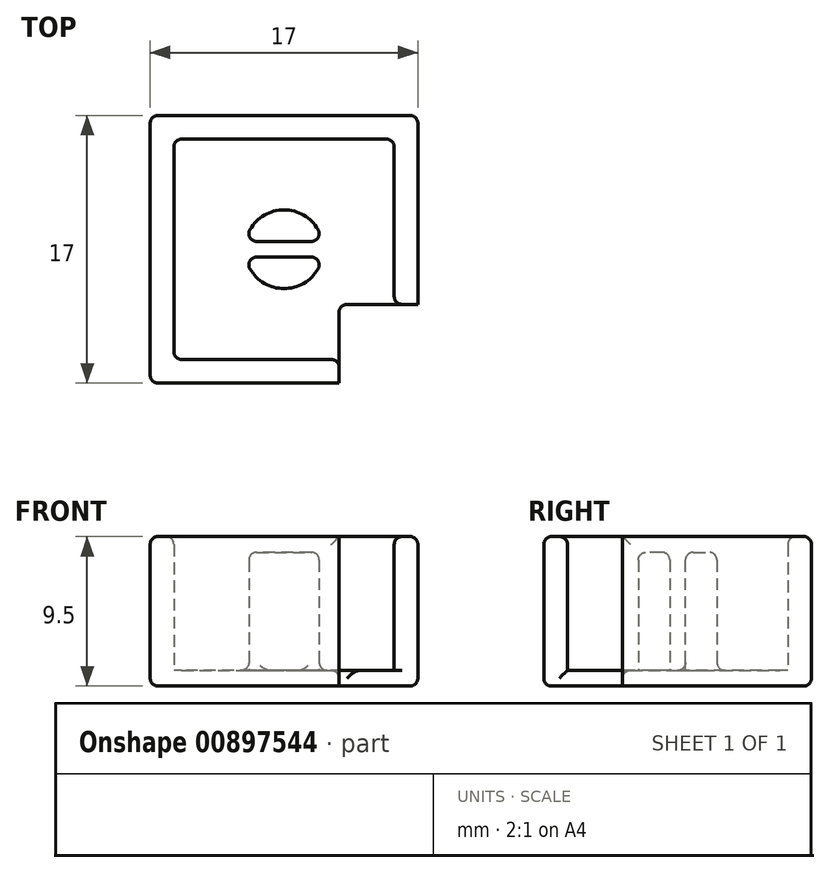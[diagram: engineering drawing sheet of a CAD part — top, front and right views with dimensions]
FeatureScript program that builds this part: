
annotation { "Feature Type Name" : "Feature", "Feature Type Description" : "" }
export const myFeature = defineFeature(function(context is Context, id is Id, definition is map)
    precondition{}
    {
        {
            var Q0;
            Q0=qCreatedBy(makeId("Top.planeOp"),FACE);
            var sketch = newSketch(context, id + "F0", { "sketchPlane" : qUnion([Q0])});
            skLineSegment(sketch, "E0.bottom", {"start": v(-42.5, 39.17) * mm, "end": v(-25.5, 39.17) * mm});
            skLineSegment(sketch, "E0.top", {"start": v(-42.5, 22.17) * mm, "end": v(-25.5, 22.17) * mm});
            skLineSegment(sketch, "E0.left", {"start": v(-42.5, 39.17) * mm, "end": v(-42.5, 22.17) * mm});
            skLineSegment(sketch, "E0.right", {"start": v(-25.5, 39.17) * mm, "end": v(-25.5, 22.17) * mm});
            skSolve(sketch);
        }
        {
            var Q0;
            Q0 = qSketchRegion(id + "F0", true);
            extrude(context, id + "F1", {"entities" : qUnion([Q0]), "depth" : 1 * mm, "offsetDistance" : 25 * mm});
        }
        {
            var Q0;
            Q0=makeQuery(id+"F1.opExtrude","CAP_FACE",FACE,{"disambiguationData":[OSD([sQuery(id+"F0.wireOp",EDGE,"E0.bottom"),sQuery(id+"F0.wireOp",EDGE,"E0.top"),sQuery(id+"F0.wireOp",EDGE,"E0.left"),sQuery(id+"F0.wireOp",EDGE,"E0.right")])],"isStart":false});
            var sketch = newSketch(context, id + "F2", { "sketchPlane" : qUnion([Q0])});
            skLineSegment(sketch, "E1.bottom", {"start": v(-42.5, 39.17) * mm, "end": v(-25.5, 39.17) * mm});
            skLineSegment(sketch, "E1.top", {"start": v(-42.5, 22.17) * mm, "end": v(-25.5, 22.17) * mm});
            skLineSegment(sketch, "E1.left", {"start": v(-42.5, 39.17) * mm, "end": v(-42.5, 22.17) * mm});
            skLineSegment(sketch, "E1.right", {"start": v(-25.5, 39.17) * mm, "end": v(-25.5, 22.17) * mm});
            skLineSegment(sketch, "E2.0", {"start": v(-41, 37.67) * mm, "end": v(-41, 23.67) * mm});
            skLineSegment(sketch, "E2.1", {"start": v(-27, 37.67) * mm, "end": v(-41, 37.67) * mm});
            skLineSegment(sketch, "E2.2", {"start": v(-27, 23.67) * mm, "end": v(-27, 37.67) * mm});
            skLineSegment(sketch, "E2.3", {"start": v(-41, 23.67) * mm, "end": v(-27, 23.67) * mm});
            skSolve(sketch);
        }
        {
            var Q0;
            Q0 = qSketchRegion(id + "F2", true);
            extrude(context, id + "F3", {"entities" : qUnion([Q0]), "operationType" : NewBodyOperationType.ADD, "depth" : 8.5 * mm, "offsetDistance" : 25 * mm});
        }
        {
            var Q0;
            Q0=makeQuery(id+"F3.boolean.opBoolean","MERGE",FACE,{"derivedFrom":[makeQuery(id+"F1.opExtrude","SWEPT_FACE",FACE,{"disambiguationData":[OSD([sQuery(id+"F0.wireOp",EDGE,"E0.top")])]}),makeQuery(id+"F3.opExtrude","SWEPT_FACE",FACE,{"disambiguationData":[OSD([sQuery(id+"F2.wireOp",EDGE,"E1.top")])]})]});
            var sketch = newSketch(context, id + "F4", { "sketchPlane" : qUnion([Q0])});
            skLineSegment(sketch, "E3.bottom", {"start": v(-30.5, 9.5) * mm, "end": v(-25.5, 9.5) * mm});
            skLineSegment(sketch, "E3.top", {"start": v(-30.5, 0) * mm, "end": v(-25.5, 0) * mm});
            skLineSegment(sketch, "E3.left", {"start": v(-30.5, 9.5) * mm, "end": v(-30.5, 0) * mm});
            skLineSegment(sketch, "E3.right", {"start": v(-25.5, 9.5) * mm, "end": v(-25.5, 0) * mm});
            skSolve(sketch);
        }
        {
            var Q0;
            Q0 = qSketchRegion(id + "F4", true);
            extrude(context, id + "F5", {"entities" : qUnion([Q0]), "operationType" : NewBodyOperationType.REMOVE, "oppositeDirection" : true, "depth" : 5 * mm, "offsetDistance" : 25 * mm});
        }
        {
            var Q0;
            Q0=makeQuery(id+"F1.opExtrude","CAP_FACE",FACE,{"disambiguationData":[OSD([sQuery(id+"F0.wireOp",EDGE,"E0.bottom"),sQuery(id+"F0.wireOp",EDGE,"E0.top"),sQuery(id+"F0.wireOp",EDGE,"E0.left"),sQuery(id+"F0.wireOp",EDGE,"E0.right")])],"isStart":false});
            var sketch = newSketch(context, id + "F6", { "sketchPlane" : qUnion([Q0])});
            skPoint(sketch, "E4.centerSnap0", {"position": v(-34, 37.67) * mm});
            skPoint(sketch, "E4.centerSnap1", {"position": v(-41, 30.67) * mm});
            skArc(sketch, "E5", {"start": v(-36.45, 30.17) * mm, "mid": v(-34, 28.17) * mm, "end": v(-31.55, 30.17) * mm});
            skLineSegment(sketch, "E6.bottom", {"start": v(-31.55, 30.17) * mm, "end": v(-36.45, 30.17) * mm});
            skLineSegment(sketch, "E6.top", {"start": v(-31.55, 31.17) * mm, "end": v(-36.45, 31.17) * mm});
            skPoint(sketch, "E6.right.end.orphan", {"position": v(-39.2, 31.17) * mm});
            skPoint(sketch, "E6.right.start.orphan", {"position": v(-39.2, 30.17) * mm});
            skPoint(sketch, "E7.orphan", {"position": v(-28.81, 31.17) * mm});
            skPoint(sketch, "E8.orphan", {"position": v(-28.81, 30.17) * mm});
            skArc(sketch, "E9.trimOffspring", {"start": v(-31.55, 31.17) * mm, "mid": v(-34, 33.17) * mm, "end": v(-36.45, 31.17) * mm});
            skSolve(sketch);
        }
        {
            var Q0;
            Q0 = qSketchRegion(id + "F6", true);
            extrude(context, id + "F7", {"entities" : qUnion([Q0]), "operationType" : NewBodyOperationType.ADD, "depth" : 7.5 * mm, "offsetDistance" : 25 * mm});
        }
        {
            var Q0;
            Q0=makeQuery(id+"F3.boolean.opBoolean","MERGE",EDGE,{"derivedFrom":[makeQuery(id+"F1.opExtrude","SWEPT_EDGE",EDGE,{"disambiguationData":[OSD([sQuery(id+"F0.wireOp",EDGE,"E0.bottom"),sQuery(id+"F0.wireOp",EDGE,"E0.left")])]}),makeQuery(id+"F3.opExtrude","SWEPT_EDGE",EDGE,{"disambiguationData":[OSD([sQuery(id+"F2.wireOp",EDGE,"E1.bottom"),sQuery(id+"F2.wireOp",EDGE,"E1.left")])]})]});
            var Q1;
            Q1=makeQuery(id+"F3.boolean.opBoolean","MERGE",EDGE,{"derivedFrom":[makeQuery(id+"F1.opExtrude","SWEPT_EDGE",EDGE,{"disambiguationData":[OSD([sQuery(id+"F0.wireOp",EDGE,"E0.top"),sQuery(id+"F0.wireOp",EDGE,"E0.left")])]}),makeQuery(id+"F3.opExtrude","SWEPT_EDGE",EDGE,{"disambiguationData":[OSD([sQuery(id+"F2.wireOp",EDGE,"E1.top"),sQuery(id+"F2.wireOp",EDGE,"E1.left")])]})]});
            var Q2;
            Q2=makeQuery(id+"F3.opExtrude","CAP_EDGE",EDGE,{"disambiguationData":[OSD([sQuery(id+"F2.wireOp",EDGE,"E1.bottom")])],"isStart":false});
            var Q3;
            Q3=makeQuery(id+"F3.opExtrude","CAP_EDGE",EDGE,{"disambiguationData":[OSD([sQuery(id+"F2.wireOp",EDGE,"E1.left")])],"isStart":false});
            var Q4;
            Q4=makeQuery(id+"F1.opExtrude","CAP_EDGE",EDGE,{"disambiguationData":[OSD([sQuery(id+"F0.wireOp",EDGE,"E0.left")])],"isStart":true});
            var Q5;
            Q5=makeQuery(id+"F1.opExtrude","CAP_EDGE",EDGE,{"disambiguationData":[OSD([sQuery(id+"F0.wireOp",EDGE,"E0.bottom")])],"isStart":true});
            var Q6;
            Q6=makeQuery(id+"F3.boolean.opBoolean","MERGE",EDGE,{"derivedFrom":[makeQuery(id+"F1.opExtrude","SWEPT_EDGE",EDGE,{"disambiguationData":[OSD([sQuery(id+"F0.wireOp",EDGE,"E0.bottom"),sQuery(id+"F0.wireOp",EDGE,"E0.right")])]}),makeQuery(id+"F3.opExtrude","SWEPT_EDGE",EDGE,{"disambiguationData":[OSD([sQuery(id+"F2.wireOp",EDGE,"E1.bottom"),sQuery(id+"F2.wireOp",EDGE,"E1.right")])]})]});
            var Q7;
            Q7=makeQuery(id+"F3.opExtrude","CAP_EDGE",EDGE,{"disambiguationData":[OSD([sQuery(id+"F2.wireOp",EDGE,"E2.1")])],"isStart":false});
            var Q8;
            Q8=makeQuery(id+"F3.opExtrude","CAP_EDGE",EDGE,{"disambiguationData":[OSD([sQuery(id+"F2.wireOp",EDGE,"E2.0")])],"isStart":false});
            var Q9;
            Q9=makeQuery(id+"F3.opExtrude","CAP_EDGE",EDGE,{"disambiguationData":[OSD([sQuery(id+"F2.wireOp",EDGE,"E2.3")])],"isStart":false});
            var Q10;
            Q10=makeQuery(id+"F3.opExtrude","CAP_EDGE",EDGE,{"disambiguationData":[OSD([sQuery(id+"F2.wireOp",EDGE,"E1.top")])],"isStart":false});
            var Q11;
            Q11=makeQuery(id+"F5.boolean.opBoolean","COPY",EDGE,{"derivedFrom":makeQuery(id+"F5.opExtrude","SWEPT_EDGE",EDGE,{"disambiguationData":[OSD([sQuery(id+"F2.wireOp",EDGE,"E1.top"),sQuery(id+"F4.wireOp",EDGE,"E3.bottom"),sQuery(id+"F4.wireOp",EDGE,"E3.left")])]})});
            var Q12;
            Q12=makeQuery(id+"F3.opExtrude","CAP_EDGE",EDGE,{"disambiguationData":[OSD([sQuery(id+"F2.wireOp",EDGE,"E2.3")])],"isStart":true});
            var Q13;
            Q13=makeQuery(id+"F3.opExtrude","SWEPT_EDGE",EDGE,{"disambiguationData":[OSD([sQuery(id+"F2.wireOp",EDGE,"E2.0"),sQuery(id+"F2.wireOp",EDGE,"E2.3")])]});
            var Q14;
            Q14=makeQuery(id+"F3.opExtrude","CAP_EDGE",EDGE,{"disambiguationData":[OSD([sQuery(id+"F2.wireOp",EDGE,"E2.0")])],"isStart":true});
            var Q15;
            Q15=makeQuery(id+"F3.opExtrude","CAP_EDGE",EDGE,{"disambiguationData":[OSD([sQuery(id+"F2.wireOp",EDGE,"E2.2")])],"isStart":true});
            var Q16;
            Q16=makeQuery(id+"F3.opExtrude","CAP_EDGE",EDGE,{"disambiguationData":[OSD([sQuery(id+"F2.wireOp",EDGE,"E2.2")])],"isStart":false});
            var Q17;
            Q17=makeQuery(id+"F3.opExtrude","CAP_EDGE",EDGE,{"disambiguationData":[OSD([sQuery(id+"F2.wireOp",EDGE,"E1.right")])],"isStart":false});
            var Q18;
            Q18=makeQuery(id+"F5.boolean.opBoolean","COPY",EDGE,{"derivedFrom":makeQuery(id+"F5.opExtrude","CAP_EDGE",EDGE,{"disambiguationData":[OSD([sQuery(id+"F4.wireOp",EDGE,"E3.bottom")])],"isStart":false})});
            var Q19;
            Q19=makeQuery(id+"F5.boolean.opBoolean","INTERSECT",EDGE,{"derivedFrom":[makeQuery(id+"F3.opExtrude","SWEPT_FACE",FACE,{"disambiguationData":[OSD([sQuery(id+"F2.wireOp",EDGE,"E2.2")])]}),makeQuery(id+"F5.opExtrude","CAP_FACE",FACE,{"disambiguationData":[OSD([sQuery(id+"F4.wireOp",EDGE,"E3.bottom"),sQuery(id+"F4.wireOp",EDGE,"E3.top"),sQuery(id+"F4.wireOp",EDGE,"E3.left"),sQuery(id+"F4.wireOp",EDGE,"E3.right")])],"isStart":false})]});
            var Q20;
            Q20=makeQuery(id+"F5.boolean.opBoolean","COPY",EDGE,{"derivedFrom":makeQuery(id+"F5.opExtrude","CAP_EDGE",EDGE,{"disambiguationData":[OSD([sQuery(id+"F4.wireOp",EDGE,"E3.right")])],"isStart":false})});
            var Q21;
            Q21=makeQuery(id+"F1.opExtrude","CAP_EDGE",EDGE,{"disambiguationData":[OSD([sQuery(id+"F0.wireOp",EDGE,"E0.top")])],"isStart":true});
            var Q22;
            Q22=makeQuery(id+"F5.boolean.opBoolean","COPY",EDGE,{"derivedFrom":makeQuery(id+"F5.opExtrude","CAP_EDGE",EDGE,{"disambiguationData":[OSD([sQuery(id+"F4.wireOp",EDGE,"E3.left")])],"isStart":true})});
            var Q23;
            Q23=makeQuery(id+"F3.opExtrude","SWEPT_EDGE",EDGE,{"disambiguationData":[OSD([sQuery(id+"F2.wireOp",EDGE,"E2.1"),sQuery(id+"F2.wireOp",EDGE,"E2.2")])]});
            var Q24;
            Q24=makeQuery(id+"F3.opExtrude","SWEPT_EDGE",EDGE,{"disambiguationData":[OSD([sQuery(id+"F2.wireOp",EDGE,"E2.0"),sQuery(id+"F2.wireOp",EDGE,"E2.1")])]});
            var Q25;
            Q25=makeQuery(id+"F7.opExtrude","CAP_EDGE",EDGE,{"disambiguationData":[OSD([sQuery(id+"F6.wireOp",EDGE,"f97c8f8d-3c43-4a7a-8bbb-6a48420f6ec5.trimOffspring")])],"isStart":false});
            var Q26;
            Q26=makeQuery(id+"F7.opExtrude","CAP_EDGE",EDGE,{"disambiguationData":[OSD([sQuery(id+"F6.wireOp",EDGE,"E4")])],"isStart":false});
            var Q27;
            Q27=makeQuery(id+"F7.opExtrude","CAP_EDGE",EDGE,{"disambiguationData":[OSD([sQuery(id+"F6.wireOp",EDGE,"E4")])],"isStart":true});
            var Q28;
            Q28=makeQuery(id+"F7.opExtrude","CAP_EDGE",EDGE,{"disambiguationData":[OSD([sQuery(id+"F6.wireOp",EDGE,"f97c8f8d-3c43-4a7a-8bbb-6a48420f6ec5.trimOffspring")])],"isStart":true});
            var Q29;
            Q29=makeQuery(id+"F5.boolean.opBoolean","COPY",EDGE,{"derivedFrom":makeQuery(id+"F5.opExtrude","SWEPT_EDGE",EDGE,{"disambiguationData":[OSD([sQuery(id+"F0.wireOp",EDGE,"E0.top"),sQuery(id+"F4.wireOp",EDGE,"E3.top"),sQuery(id+"F4.wireOp",EDGE,"E3.left")])]})});
            var Q30;
            Q30=makeQuery(id+"F5.boolean.opBoolean","INTERSECT",EDGE,{"derivedFrom":[makeQuery(id+"F1.opExtrude","CAP_FACE",FACE,{"disambiguationData":[OSD([sQuery(id+"F0.wireOp",EDGE,"E0.bottom"),sQuery(id+"F0.wireOp",EDGE,"E0.top"),sQuery(id+"F0.wireOp",EDGE,"E0.left"),sQuery(id+"F0.wireOp",EDGE,"E0.right")])],"isStart":false}),makeQuery(id+"F5.opExtrude","SWEPT_FACE",FACE,{"disambiguationData":[OSD([sQuery(id+"F4.wireOp",EDGE,"E3.left")])]})]});
            var Q31;
            Q31=makeQuery(id+"F5.boolean.opBoolean","COPY",EDGE,{"derivedFrom":makeQuery(id+"F5.opExtrude","CAP_EDGE",EDGE,{"disambiguationData":[OSD([sQuery(id+"F4.wireOp",EDGE,"E3.top")])],"isStart":false})});
            var Q32;
            Q32=makeQuery(id+"F1.opExtrude","CAP_EDGE",EDGE,{"disambiguationData":[OSD([sQuery(id+"F0.wireOp",EDGE,"E0.right")])],"isStart":true});
            var Q33;
            Q33=makeQuery(id+"F5.boolean.opBoolean","INTERSECT",EDGE,{"derivedFrom":[makeQuery(id+"F3.opExtrude","SWEPT_FACE",FACE,{"disambiguationData":[OSD([sQuery(id+"F2.wireOp",EDGE,"E2.3")])]}),makeQuery(id+"F5.opExtrude","SWEPT_FACE",FACE,{"disambiguationData":[OSD([sQuery(id+"F4.wireOp",EDGE,"E3.left")])]})]});
            var Q34;
            Q34=makeQuery(id+"F5.boolean.opBoolean","COPY",EDGE,{"derivedFrom":makeQuery(id+"F5.opExtrude","CAP_EDGE",EDGE,{"disambiguationData":[OSD([sQuery(id+"F4.wireOp",EDGE,"E3.left")])],"isStart":false})});
            var Q35;
            {var subQ0=sQuery(id+"F6.wireOp",EDGE,"f97c8f8d-3c43-4a7a-8bbb-6a48420f6ec5.trimOffspring");var subQ1=sQuery(id+"F6.wireOp",EDGE,"y5B7XSze-Zx87-gcmj-TOVZ-qQVviGRR6gWb");Q35=makeQuery(id+"F7.opExtrude","SWEPT_EDGE",EDGE,{"disambiguationData":[OSD([subQ1,subQ0]),TDD([makeQuery(id+"F6.imprint","INTERSECT",VERTEX,{"disambiguationData":[OD(1.0)],"derivedFrom":[subQ1,subQ0]})])]});}
            var Q36;
            {var subQ0=sQuery(id+"F6.wireOp",EDGE,"laSpJind-ru56-Ced7-BBqZ-NThufxKhyAuO");var subQ1=sQuery(id+"F6.wireOp",EDGE,"E4");Q36=makeQuery(id+"F7.opExtrude","SWEPT_EDGE",EDGE,{"disambiguationData":[OSD([subQ1,subQ0]),TDD([makeQuery(id+"F6.imprint","INTERSECT",VERTEX,{"disambiguationData":[OD(1.0)],"derivedFrom":[subQ1,subQ0]})])]});}
            var Q37;
            Q37=makeQuery(id+"F7.opExtrude","CAP_EDGE",EDGE,{"disambiguationData":[OSD([sQuery(id+"F6.wireOp",EDGE,"laSpJind-ru56-Ced7-BBqZ-NThufxKhyAuO")])],"isStart":false});
            var Q38;
            Q38=makeQuery(id+"F7.opExtrude","CAP_EDGE",EDGE,{"disambiguationData":[OSD([sQuery(id+"F6.wireOp",EDGE,"y5B7XSze-Zx87-gcmj-TOVZ-qQVviGRR6gWb")])],"isStart":false});
            var Q39;
            {var subQ0=sQuery(id+"F6.wireOp",EDGE,"f97c8f8d-3c43-4a7a-8bbb-6a48420f6ec5.trimOffspring");var subQ1=sQuery(id+"F6.wireOp",EDGE,"y5B7XSze-Zx87-gcmj-TOVZ-qQVviGRR6gWb");Q39=makeQuery(id+"F7.opExtrude","SWEPT_EDGE",EDGE,{"disambiguationData":[OSD([subQ1,subQ0]),TDD([makeQuery(id+"F6.imprint","INTERSECT",VERTEX,{"disambiguationData":[OD(0.0)],"derivedFrom":[subQ1,subQ0]})])]});}
            var Q40;
            {var subQ0=sQuery(id+"F6.wireOp",EDGE,"laSpJind-ru56-Ced7-BBqZ-NThufxKhyAuO");var subQ1=sQuery(id+"F6.wireOp",EDGE,"E4");Q40=makeQuery(id+"F7.opExtrude","SWEPT_EDGE",EDGE,{"disambiguationData":[OSD([subQ1,subQ0]),TDD([makeQuery(id+"F6.imprint","INTERSECT",VERTEX,{"disambiguationData":[OD(0.0)],"derivedFrom":[subQ1,subQ0]})])]});}
            fillet(context, id + "F8", {"entities" : qUnion([Q0, Q1, Q2, Q3, Q4, Q5, Q6, Q7, Q8, Q9, Q10, Q11, Q12, Q13, Q14, Q15, Q16, Q17, Q18, Q19, Q20, Q21, Q22, Q23, Q24, Q25, Q26, Q27, Q28, Q29, Q30, Q31, Q32, Q33, Q34, Q35, Q36, Q37, Q38, Q39, Q40]), "radius" : 0.5 * mm, "tangentPropagation" : true, "allowEdgeOverflow" : false});
        }
        {
            var Q0;
            Q0=makeQuery(id+"F7.opExtrude","CAP_EDGE",EDGE,{"disambiguationData":[OSD([sQuery(id+"F6.wireOp",EDGE,"E9.trimOffspring")])],"isStart":false});
            var Q1;
            Q1=makeQuery(id+"F7.opExtrude","CAP_EDGE",EDGE,{"disambiguationData":[OSD([sQuery(id+"F6.wireOp",EDGE,"E6.top")])],"isStart":false});
            var Q2;
            Q2=makeQuery(id+"F7.opExtrude","CAP_EDGE",EDGE,{"disambiguationData":[OSD([sQuery(id+"F6.wireOp",EDGE,"E6.bottom")])],"isStart":false});
            var Q3;
            Q3=makeQuery(id+"F7.opExtrude","CAP_EDGE",EDGE,{"disambiguationData":[OSD([sQuery(id+"F6.wireOp",EDGE,"E5")])],"isStart":false});
            var Q4;
            {var subQ0=sQuery(id+"F6.wireOp",EDGE,"E9.trimOffspring");var subQ1=sQuery(id+"F6.wireOp",EDGE,"E6.top");Q4=makeQuery(id+"F7.opExtrude","SWEPT_EDGE",EDGE,{"disambiguationData":[OSD([subQ1,subQ0]),TDD([makeQuery(id+"F6.imprint","INTERSECT",VERTEX,{"disambiguationData":[OD(0.0)],"derivedFrom":[subQ1,subQ0]})])]});}
            var Q5;
            {var subQ0=sQuery(id+"F6.wireOp",EDGE,"E6.bottom");var subQ1=sQuery(id+"F6.wireOp",EDGE,"E5");Q5=makeQuery(id+"F7.opExtrude","SWEPT_EDGE",EDGE,{"disambiguationData":[OSD([subQ1,subQ0]),TDD([makeQuery(id+"F6.imprint","INTERSECT",VERTEX,{"disambiguationData":[OD(1.0)],"derivedFrom":[subQ1,subQ0]})])]});}
            var Q6;
            Q6=makeQuery(id+"F7.opExtrude","CAP_EDGE",EDGE,{"disambiguationData":[OSD([sQuery(id+"F6.wireOp",EDGE,"E5")])],"isStart":true});
            var Q7;
            {var subQ0=sQuery(id+"F6.wireOp",EDGE,"E6.bottom");var subQ1=sQuery(id+"F6.wireOp",EDGE,"E5");Q7=makeQuery(id+"F7.opExtrude","SWEPT_EDGE",EDGE,{"disambiguationData":[OSD([subQ1,subQ0]),TDD([makeQuery(id+"F6.imprint","INTERSECT",VERTEX,{"disambiguationData":[OD(0.0)],"derivedFrom":[subQ1,subQ0]})])]});}
            var Q8;
            Q8=makeQuery(id+"F7.opExtrude","SWEPT_FACE",FACE,{"disambiguationData":[OSD([sQuery(id+"F6.wireOp",EDGE,"E9.trimOffspring")])]});
            fillet(context, id + "F9", {"entities" : qUnion([Q0, Q1, Q2, Q3, Q4, Q5, Q6, Q7, Q8]), "radius" : 0.5 * mm, "tangentPropagation" : true, "allowEdgeOverflow" : false});
        }
    });
